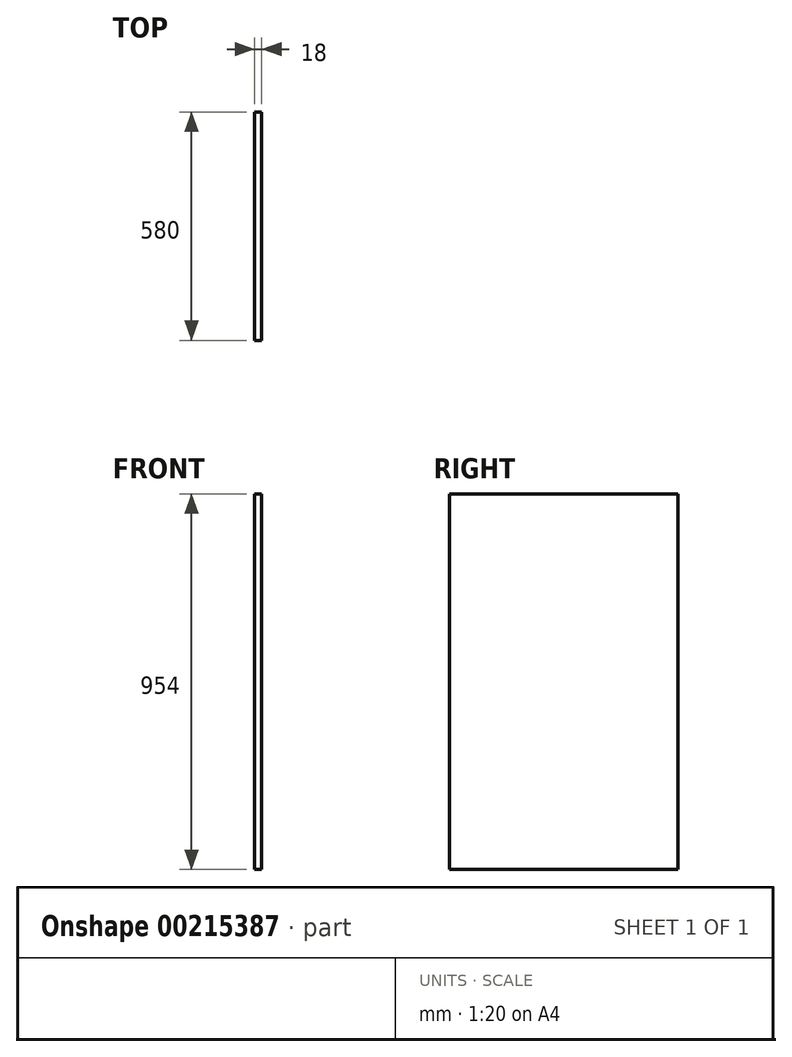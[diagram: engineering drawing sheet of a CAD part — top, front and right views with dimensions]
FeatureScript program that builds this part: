
annotation { "Feature Type Name" : "Feature", "Feature Type Description" : "" }
export const myFeature = defineFeature(function(context is Context, id is Id, definition is map)
    precondition{}
    {
        {
            var Q0;
            Q0=qCreatedBy(makeId("Right.planeOp"),FACE);
            var sketch = newSketch(context, id + "F0", { "sketchPlane" : qUnion([Q0])});
            skLineSegment(sketch, "E0.bottom", {"start": v(-290, -477) * mm, "end": v(290, -477) * mm});
            skLineSegment(sketch, "E0.top", {"start": v(-290, 477) * mm, "end": v(290, 477) * mm});
            skLineSegment(sketch, "E0.left", {"start": v(-290, -477) * mm, "end": v(-290, 477) * mm});
            skLineSegment(sketch, "E0.right", {"start": v(290, -477) * mm, "end": v(290, 477) * mm});
            skPoint(sketch, "E0.middle", {"position": v(0, 0) * mm});
            skSolve(sketch);
        }
        {
            var Q0;
            Q0=qSketchRegion(id+"F0",true);
            extrude(context, id + "F1", {"entities" : qUnion([Q0]), "depth" : 18 * mm});
        }
    });
